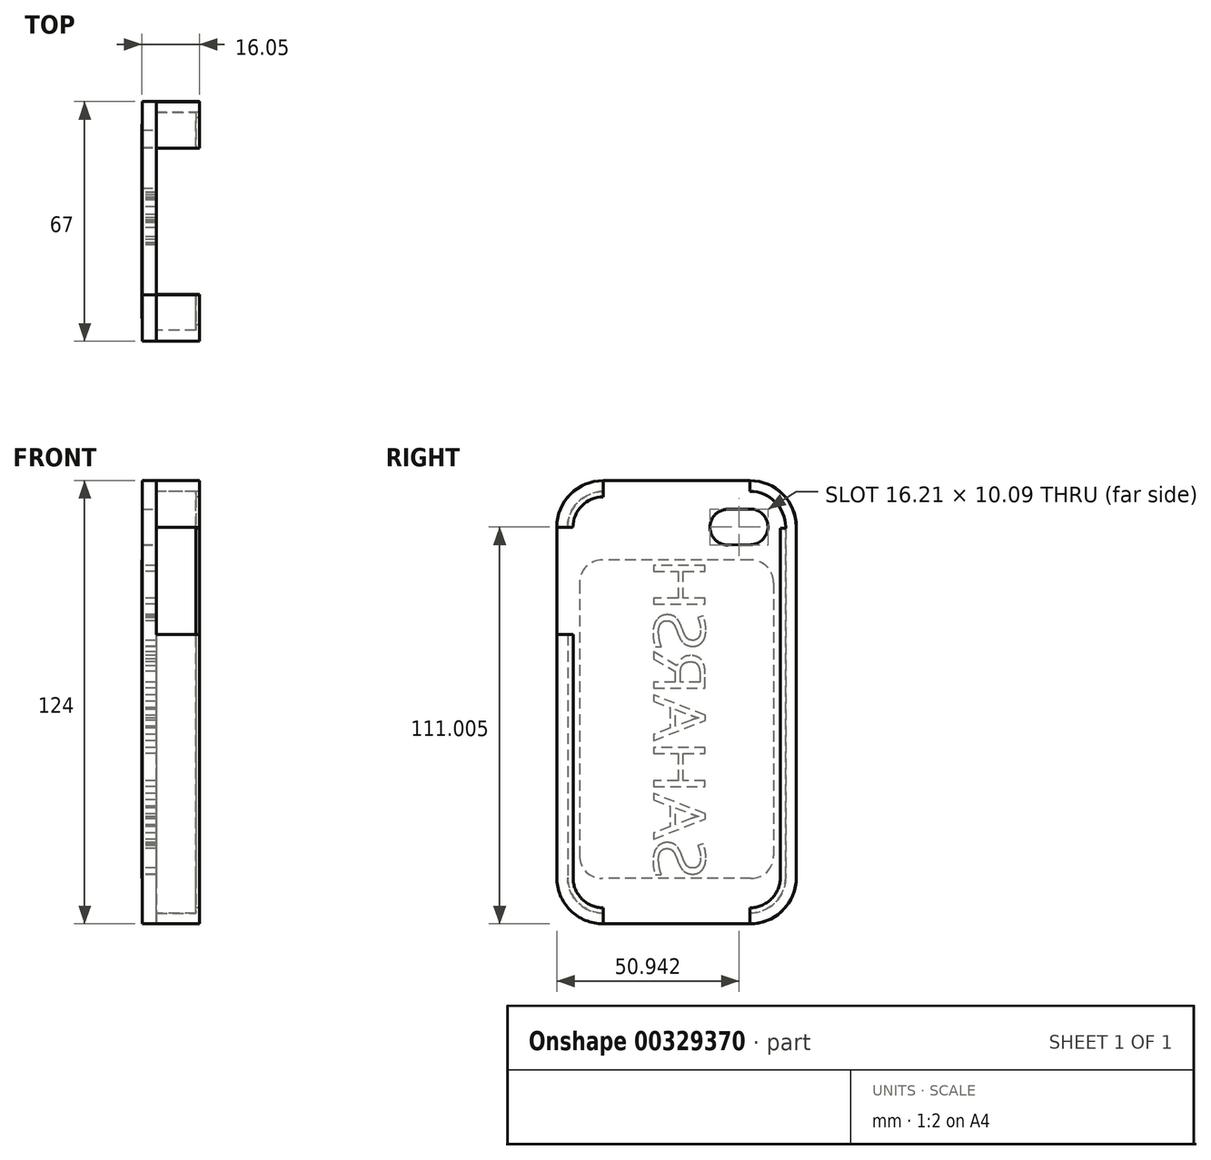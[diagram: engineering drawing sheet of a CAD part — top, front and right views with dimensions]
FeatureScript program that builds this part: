
annotation { "Feature Type Name" : "Feature", "Feature Type Description" : "" }
export const myFeature = defineFeature(function(context is Context, id is Id, definition is map)
    precondition{}
    {
        {
            var Q0;
            Q0=qCreatedBy(makeId("Right.planeOp"),FACE);
            var sketch = newSketch(context, id + "F0", { "sketchPlane" : qUnion([Q0])});
            skLineSegment(sketch, "E0.rect.bottom", {"start": v(20.5, 62) * mm, "end": v(-20.5, 62) * mm});
            skLineSegment(sketch, "E0.rect.top", {"start": v(20.5, -62) * mm, "end": v(-20.5, -62) * mm});
            skLineSegment(sketch, "E0.rect.left", {"start": v(33.5, 49) * mm, "end": v(33.5, -49) * mm});
            skLineSegment(sketch, "E0.rect.right", {"start": v(-33.5, 49) * mm, "end": v(-33.5, -49) * mm});
            skPoint(sketch, "E0.rect.middle", {"position": v(0, 0) * mm});
            skPoint(sketch, "E1.visualSharp", {"position": v(-33.5, 62) * mm});
            skArc(sketch, "E1.filletArc", {"start": v(-20.5, 62) * mm, "mid": v(-29.7, 58.2) * mm, "end": v(-33.5, 49) * mm});
            skPoint(sketch, "E2.visualSharp", {"position": v(-33.5, -62) * mm});
            skArc(sketch, "E2.filletArc", {"start": v(-33.5, -49) * mm, "mid": v(-29.7, -58.2) * mm, "end": v(-20.5, -62) * mm});
            skPoint(sketch, "E3.visualSharp", {"position": v(33.5, 62) * mm});
            skArc(sketch, "E3.filletArc", {"start": v(33.5, 49) * mm, "mid": v(29.7, 58.2) * mm, "end": v(20.5, 62) * mm});
            skPoint(sketch, "E4.visualSharp", {"position": v(33.5, -62) * mm});
            skArc(sketch, "E4.filletArc", {"start": v(20.5, -62) * mm, "mid": v(29.7, -58.2) * mm, "end": v(33.5, -49) * mm});
            skSolve(sketch);
        }
        {
            var Q0;
            Q0=qSketchRegion(id+"F0",true);
            extrude(context, id + "F1", {"entities" : qUnion([Q0]), "depth" : 4 * mm});
        }
        {
            var Q0;
            Q0=qCreatedBy(makeId("Right.planeOp"),FACE);
            var sketch = newSketch(context, id + "F2", { "sketchPlane" : qUnion([Q0])});
            skArc(sketch, "E5", {"start": v(20.7, 44.05) * mm, "mid": v(25.55, 49.12) * mm, "end": v(20.55, 54.05) * mm});
            skLineSegment(sketch, "E6", {"start": v(20.55, 54.05) * mm, "end": v(14.26, 53.96) * mm});
            skLineSegment(sketch, "E7", {"start": v(20.7, 44.05) * mm, "end": v(14.4, 43.96) * mm});
            skArc(sketch, "E8", {"start": v(14.26, 53.96) * mm, "mid": v(9.34, 48.89) * mm, "end": v(14.4, 43.96) * mm});
            skLineSegment(sketch, "E9", {"start": v(14.26, 53.96) * mm, "end": v(14.4, 43.96) * mm, "construction": true});
            skLineSegment(sketch, "E10", {"start": v(20.55, 54.05) * mm, "end": v(20.7, 44.05) * mm, "construction": true});
            skSolve(sketch);
        }
        {
            var Q0;
            Q0=makeQuery(id+"F2.imprint","IMPRINT",FACE,{"disambiguationData":[TD([[makeQuery(id+"F2.imprint","IMPRINT",EDGE,{"derivedFrom":sQuery(id+"F2.wireOp",EDGE,"E5")}),1.0]])]});
            extrude(context, id + "F3", {"entities" : qUnion([Q0]), "operationType" : NewBodyOperationType.REMOVE, "oppositeDirection" : true, "depth" : 25.4 * mm, "hasSecondDirection" : true, "secondDirectionOppositeDirection" : false, "secondDirectionDepth" : 33.72 * mm});
        }
        {
            var Q0;
            Q0=qCreatedBy(makeId("Right.planeOp"),FACE);
            var sketch = newSketch(context, id + "F4", { "sketchPlane" : qUnion([Q0])});
            skLineSegment(sketch, "E11", {"start": v(-30.46, 18.92) * mm, "end": v(-33.5, 18.92) * mm});
            skLineSegment(sketch, "E12", {"start": v(-33.5, 18.92) * mm, "end": v(-33.5, -49) * mm});
            skLineSegment(sketch, "E13", {"start": v(-33.5, -49) * mm, "end": v(-30.46, -49) * mm});
            skLineSegment(sketch, "E14", {"start": v(-30.46, -49) * mm, "end": v(-30.46, 18.92) * mm});
            skSolve(sketch);
        }
        {
            var Q0;
            Q0=qSketchRegion(id+"F4",true);
            extrude(context, id + "F5", {"entities" : qUnion([Q0]), "operationType" : NewBodyOperationType.ADD, "depth" : 16 * mm});
        }
        {
            var Q0;
            Q0=qCreatedBy(makeId("Right.planeOp"),FACE);
            var sketch = newSketch(context, id + "F6", { "sketchPlane" : qUnion([Q0])});
            skLineSegment(sketch, "E15", {"start": v(-33.5, -49) * mm, "end": v(-30.46, -49) * mm});
            skLineSegment(sketch, "E16", {"start": v(-20.5, -59) * mm, "end": v(-20.5, -62) * mm});
            skArc(sketch, "E17", {"start": v(-30.46, -49) * mm, "mid": v(-27.56, -56.07) * mm, "end": v(-20.5, -59) * mm});
            skArc(sketch, "E18", {"start": v(-33.5, -49) * mm, "mid": v(-29.7, -58.2) * mm, "end": v(-20.5, -62) * mm});
            skSolve(sketch);
        }
        {
            var Q0;
            Q0=qSketchRegion(id+"F6",true);
            extrude(context, id + "F7", {"entities" : qUnion([Q0]), "operationType" : NewBodyOperationType.ADD, "depth" : 16 * mm});
        }
        {
            var Q0;
            Q0=qCreatedBy(makeId("Right.planeOp"),FACE);
            var sketch = newSketch(context, id + "F8", { "sketchPlane" : qUnion([Q0])});
            skLineSegment(sketch, "E19", {"start": v(-30.47, 48.93) * mm, "end": v(-33.5, 48.93) * mm});
            skLineSegment(sketch, "E20", {"start": v(-20.5, 62) * mm, "end": v(-20.5, 58.97) * mm});
            skArc(sketch, "E21", {"start": v(-20.5, 58.97) * mm, "mid": v(-27.55, 56) * mm, "end": v(-30.47, 48.93) * mm});
            skArc(sketch, "E22", {"start": v(-20.5, 62) * mm, "mid": v(-29.7, 58.15) * mm, "end": v(-33.5, 48.93) * mm});
            skSolve(sketch);
        }
        {
            var Q0;
            Q0=qSketchRegion(id+"F8",true);
            extrude(context, id + "F9", {"entities" : qUnion([Q0]), "operationType" : NewBodyOperationType.ADD, "depth" : 16 * mm});
        }
        {
            var Q0;
            Q0=qCreatedBy(makeId("Right.planeOp"),FACE);
            var sketch = newSketch(context, id + "F10", { "sketchPlane" : qUnion([Q0])});
            skLineSegment(sketch, "E23", {"start": v(20.49, -62) * mm, "end": v(20.49, -59) * mm});
            skLineSegment(sketch, "E24", {"start": v(33.5, -49) * mm, "end": v(30.5, -49) * mm});
            skArc(sketch, "E25", {"start": v(20.49, -59) * mm, "mid": v(27.55, -56.06) * mm, "end": v(30.5, -49) * mm});
            skArc(sketch, "E26", {"start": v(20.49, -62) * mm, "mid": v(29.67, -58.19) * mm, "end": v(33.5, -49) * mm});
            skSolve(sketch);
        }
        {
            var Q0;
            Q0=qSketchRegion(id+"F10",true);
            extrude(context, id + "F11", {"entities" : qUnion([Q0]), "operationType" : NewBodyOperationType.ADD, "depth" : 16 * mm});
        }
        {
            var Q0;
            Q0=qCreatedBy(makeId("Right.planeOp"),FACE);
            var sketch = newSketch(context, id + "F12", { "sketchPlane" : qUnion([Q0])});
            skLineSegment(sketch, "E27", {"start": v(33.46, 49) * mm, "end": v(30.5, 49) * mm});
            skLineSegment(sketch, "E28", {"start": v(20.5, 62) * mm, "end": v(20.5, 58.99) * mm});
            skArc(sketch, "E29", {"start": v(33.46, 49) * mm, "mid": v(29.66, 58.17) * mm, "end": v(20.5, 62) * mm});
            skArc(sketch, "E30", {"start": v(30.5, 49) * mm, "mid": v(27.55, 56.05) * mm, "end": v(20.5, 58.99) * mm});
            skSolve(sketch);
        }
        {
            var Q0;
            Q0=qSketchRegion(id+"F12",true);
            extrude(context, id + "F13", {"entities" : qUnion([Q0]), "operationType" : NewBodyOperationType.ADD, "depth" : 16 * mm});
        }
        {
            var Q0;
            Q0=qCreatedBy(makeId("Right.planeOp"),FACE);
            var sketch = newSketch(context, id + "F14", { "sketchPlane" : qUnion([Q0])});
            skLineSegment(sketch, "E31", {"start": v(30.5, -49) * mm, "end": v(33.49, -49) * mm});
            skLineSegment(sketch, "E32", {"start": v(33.49, -49) * mm, "end": v(33.49, 49) * mm});
            skLineSegment(sketch, "E33", {"start": v(33.49, 49) * mm, "end": v(30.5, 49) * mm});
            skLineSegment(sketch, "E34", {"start": v(30.5, 49) * mm, "end": v(30.5, -49) * mm});
            skSolve(sketch);
        }
        {
            var Q0;
            Q0=qSketchRegion(id+"F14",true);
            extrude(context, id + "F15", {"entities" : qUnion([Q0]), "operationType" : NewBodyOperationType.ADD, "depth" : 16 * mm});
        }
        {
            var Q0;
            Q0=qCreatedBy(makeId("Right.planeOp"),FACE);
            var sketch = newSketch(context, id + "F16", { "sketchPlane" : qUnion([Q0])});
            skLineSegment(sketch, "E35", {"start": v(-30.46, 18.92) * mm, "end": v(-30.46, -49.07) * mm});
            skLineSegment(sketch, "E36", {"start": v(-30.46, -49.07) * mm, "end": v(-28.96, -49.07) * mm});
            skLineSegment(sketch, "E37", {"start": v(-28.96, -49.07) * mm, "end": v(-28.96, 18.92) * mm});
            skLineSegment(sketch, "E38", {"start": v(-28.96, 18.92) * mm, "end": v(-30.46, 18.92) * mm});
            skLineSegment(sketch, "E39", {"start": v(-20.5, -59) * mm, "end": v(-20.5, -57.5) * mm});
            skArc(sketch, "E40", {"start": v(-30.46, -49.07) * mm, "mid": v(-27.53, -56.1) * mm, "end": v(-20.5, -59) * mm});
            skArc(sketch, "E41", {"start": v(-28.96, -49.07) * mm, "mid": v(-26.47, -55.04) * mm, "end": v(-20.5, -57.5) * mm});
            skLineSegment(sketch, "E42", {"start": v(-30.47, 48.93) * mm, "end": v(-28.97, 48.93) * mm});
            skLineSegment(sketch, "E43", {"start": v(-20.5, 58.97) * mm, "end": v(-20.5, 57.47) * mm});
            skArc(sketch, "E44", {"start": v(-20.5, 58.97) * mm, "mid": v(-27.55, 56) * mm, "end": v(-30.47, 48.93) * mm});
            skArc(sketch, "E45", {"start": v(-20.5, 57.47) * mm, "mid": v(-26.5, 54.95) * mm, "end": v(-28.97, 48.93) * mm});
            skLineSegment(sketch, "E46", {"start": v(30.5, 48.62) * mm, "end": v(29, 48.62) * mm});
            skLineSegment(sketch, "E47", {"start": v(30.5, -49) * mm, "end": v(29, -49) * mm});
            skLineSegment(sketch, "E48", {"start": v(29, -49) * mm, "end": v(29, 48.62) * mm});
            skLineSegment(sketch, "E49", {"start": v(30.5, 48.62) * mm, "end": v(30.5, -49) * mm});
            skLineSegment(sketch, "E50", {"start": v(20.49, -59) * mm, "end": v(20.49, -57.5) * mm});
            skArc(sketch, "E51", {"start": v(20.49, -59) * mm, "mid": v(27.54, -56.06) * mm, "end": v(30.5, -49) * mm});
            skArc(sketch, "E52", {"start": v(20.49, -57.5) * mm, "mid": v(26.5, -55.02) * mm, "end": v(29, -49) * mm});
            skSolve(sketch);
        }
        {
            var Q0;
            Q0=qSketchRegion(id+"F16",true);
            extrude(context, id + "F17", {"entities" : qUnion([Q0]), "operationType" : NewBodyOperationType.ADD, "depth" : 16 * mm, "hasSecondDirection" : true, "secondDirectionOppositeDirection" : false, "secondDirectionDepth" : 15 * mm});
        }
        {
            var Q0;
            Q0=makeQuery(id+"F7.boolean.opBoolean","MERGE",FACE,{"derivedFrom":[makeQuery(id+"F1.opExtrude","CAP_FACE",FACE,{"disambiguationData":[OSD([sQuery(id+"F0.wireOp",EDGE,"E0.rect.bottom"),sQuery(id+"F0.wireOp",EDGE,"E0.rect.top"),sQuery(id+"F0.wireOp",EDGE,"E0.rect.left"),sQuery(id+"F0.wireOp",EDGE,"E0.rect.right"),sQuery(id+"F0.wireOp",EDGE,"E1.filletArc"),sQuery(id+"F0.wireOp",EDGE,"E2.filletArc"),sQuery(id+"F0.wireOp",EDGE,"E3.filletArc"),sQuery(id+"F0.wireOp",EDGE,"E4.filletArc")])],"isStart":true}),makeQuery(id+"F7.opExtrude","CAP_FACE",FACE,{"disambiguationData":[OSD([sQuery(id+"F6.wireOp",EDGE,"E15"),sQuery(id+"F6.wireOp",EDGE,"E16"),sQuery(id+"F6.wireOp",EDGE,"E17"),sQuery(id+"F6.wireOp",EDGE,"E18")])],"isStart":true})]});
            var sketch = newSketch(context, id + "F18", { "sketchPlane" : qUnion([Q0])});
            skLineSegment(sketch, "E53.bottom", {"start": v(-20.8, 39.78) * mm, "end": v(20.8, 39.78) * mm});
            skLineSegment(sketch, "E53.top", {"start": v(-20.8, -49.3) * mm, "end": v(20.8, -49.3) * mm});
            skLineSegment(sketch, "E53.left", {"start": v(-27.15, 33.43) * mm, "end": v(-27.15, -42.95) * mm});
            skLineSegment(sketch, "E53.right", {"start": v(27.15, 33.42) * mm, "end": v(27.15, -42.95) * mm});
            skPoint(sketch, "E54.visualSharp", {"position": v(-27.15, 39.78) * mm});
            skArc(sketch, "E54.filletArc", {"start": v(-20.8, 39.78) * mm, "mid": v(-25.3, 37.92) * mm, "end": v(-27.15, 33.43) * mm});
            skPoint(sketch, "E55.visualSharp", {"position": v(-27.15, -49.3) * mm});
            skArc(sketch, "E55.filletArc", {"start": v(-27.15, -42.95) * mm, "mid": v(-25.3, -47.44) * mm, "end": v(-20.8, -49.3) * mm});
            skPoint(sketch, "E56.visualSharp", {"position": v(27.15, -49.3) * mm});
            skArc(sketch, "E56.filletArc", {"start": v(20.8, -49.3) * mm, "mid": v(25.3, -47.44) * mm, "end": v(27.15, -42.95) * mm});
            skPoint(sketch, "E57.visualSharp", {"position": v(27.15, 39.78) * mm});
            skArc(sketch, "E57.filletArc", {"start": v(27.15, 33.42) * mm, "mid": v(25.3, 37.92) * mm, "end": v(20.8, 39.78) * mm});
            skSolve(sketch);
        }
        {
            var Q0;
            Q0=qSketchRegion(id+"F18",true);
            extrude(context, id + "F19", {"entities" : qUnion([Q0]), "operationType" : NewBodyOperationType.ADD, "depth" : 0.05 * mm});
        }
        {
            var Q0;
            Q0=makeQuery(id+"F19.opExtrude","CAP_FACE",FACE,{"disambiguationData":[OSD([sQuery(id+"F18.wireOp",EDGE,"E53.bottom"),sQuery(id+"F18.wireOp",EDGE,"E53.top"),sQuery(id+"F18.wireOp",EDGE,"E53.left"),sQuery(id+"F18.wireOp",EDGE,"E53.right"),sQuery(id+"F18.wireOp",EDGE,"E54.filletArc"),sQuery(id+"F18.wireOp",EDGE,"E55.filletArc"),sQuery(id+"F18.wireOp",EDGE,"E56.filletArc"),sQuery(id+"F18.wireOp",EDGE,"E57.filletArc")])],"isStart":false});
            var sketch = newSketch(context, id + "F20", { "sketchPlane" : qUnion([Q0])});
            skText(sketch, "E58", { "text": "SAHARSH", "fontName": "OpenSans-Regular.ttf"});
            const initialGuessF20  = {"E58": [0.00637, -0.0493, 0, 1, 0.01447]};
            skSetInitialGuess(sketch, initialGuessF20);
            skSolve(sketch);
        }
        {
            var Q0;
            Q0=qSketchRegion(id+"F20",true);
            extrude(context, id + "F21", {"entities" : qUnion([Q0]), "operationType" : NewBodyOperationType.REMOVE, "oppositeDirection" : true, "depth" : 4 * mm});
        }
    });
